# Revit family: NEC PA571W but PA550W before -DONE
name_source: partatom
category: Generic Models
revit_build: Autodesk Revit Architecture 2012 (Build: 20110309_2315(x64)
units: mm (PartAtom-declared; Revit-internal decimal feet)

## types (1)
- NEC PA571W but PA550W before -DONE
    Accessories - NP02CV = Terminal Cover
    Accessories - NP02LM1 = Wireless LAN module
    Accessories - NP11FL = 0.8 : 1 fixed short throw lens
    Accessories - NP12ZL = 1.19 - 1.56 : 1 zoom lens
    Accessories - NP13ZL = 1.5 - 3.0 : 1 zoom lens
    Accessories - NP14ZL = 2.97 - 4.79 : 1 zoom lens
    Accessories - NP15ZL = 4.7- 7.2 : 1 zoom lens
    Accessories - NP21LP = Replacement lamp
    Accessories - NP3250CM = Ceiling mount
    Accessories - PW RCRD-PJPX = Power Cable
    Accessories - RGBCBL-PJPX = RGB Cable
    Accessories - RMT-PJ33 = Remote remote control
    Accessories - SCP200 = Suspended ceiling plate
    Dimensions (W x D x H) = 19.6 x 14.1 x 5.7 in / 499 x 359 x 144 mm
    Environmental - Humidity = 20-80% non-condensing
    Environmental - Operational Temp = 41deg - 104degF / 5deg - 40degC
    Environmental - Storage = 14deg - 122degF / -10deg - 50degC
    Fan Noise = 38 dB normal / 31 dB eco
    Input Current = 5.1A
    Installation Orientation = Floor/Front, Floor/Rear, Ceiling/Front, Ceiling/Rear
    Manufacturer = NEC Display Solutions
    Model = PA500X
    Net Weight = 17.6 lb / 8 kg
    New Features = Portrait Orientation, Tilt free, 3D
    Optical - Contrast Ratio = 2000 : 1 with auto iris
    Optical - Display Technology = 0.75" LCD with MLA
    Optical - Lamp Life (up to) = 3000 hrs normal / 4000 hrs eco
    Optical - Lamp Type = 330W AC
    Optical - Lens F-number = F = 1.7 to 2.2, f = 24.4 to 32.5mm
    Optical - Lens Keystone Correction = +/- 40 deg horizontal, +/- 30 deg vertical
    Optical - Lens Shift = mechanical -0.1 to +0.6 vertical, +/-0.3 horizontal
    Optical - Lens Zoom = 1 to 1.33
    Optical - Lens focus = Manual
    Optical - Maximum Light Output (lumens) = 5700 Normal
    Optical - Projection Angle = 10.3 to 10.8deg tele / 13.7 to 14.5deg wide
    Optical - Projection Distance = 2.5 to 68.5ft, 0.74 to 20.9m
    Optical - Resolution, Native = WXGA 1280 x 800
    Optical - Screen Size (diagonal) = 25 to 500in, 635 to 12,700mm
    Optical - Throw Ratio = 1.5 to 3 (standard lens)
    Power Consumption (Normal/Eco Mode/Standby/Netwrok Standby/Power Saving) = 464W / 372W / 16W / 6W / 0.2W
    Power Requirements = 100-240V AC, 50/60Hz
    Regulations = USA UL 1950 FCC Class B, Canada CSA950 (C-UL), NOM
    Signal Compatibility/Connectivity - Audio = 10W mono
    Signal Compatibility/Connectivity - External Control = RS-232, IR
    Signal Compatibility/Connectivity - Input/Output Terminals  Audio = (2) L/R RCA, (3) mini stereo
    Signal Compatibility/Connectivity - Input/Output Terminals  Audio Out = mini VAO
    Signal Compatibility/Connectivity - Input/Output Terminals  Monitor Out = Yes
    Signal Compatibility/Connectivity - Input/Output Terminals  RGB1 (analog) = 15 pin
    Signal Compatibility/Connectivity - Input/Output Terminals  RGB2 (analog) = 15 pin
    Signal Compatibility/Connectivity - Input/Output Terminals  RGB3 (analog) = 5-BNC
    Signal Compatibility/Connectivity - Input/Output Terminals  RGB4 (digital) = Dual HDMI w/ HDCP
    Signal Compatibility/Connectivity - Input/Output Terminals  RGB5 (digital) = DisplayPort
    Signal Compatibility/Connectivity - Input/Output Terminals  Video 1 = RCA
    Signal Compatibility/Connectivity - Input/Output Terminals  Video 2 = S-Video
    Signal Compatibility/Connectivity - Macintosh Compatibility = Yes
    Signal Compatibility/Connectivity - PC Signal Compatibility = VGA, SVGA, XGA, SXGA, SXGA+, UXGA
    Signal Compatibility/Connectivity - SD/HD Video Signal Compatibility = 1080p, 1080i, 720p, 576p, 576i, 480p, 480i
    Signal Compatibility/Connectivity - Scan Rate = Horizontal 15-108 kHz / Vertical 48 - 120 Hz
    Signal Compatibility/Connectivity - Supported Video Standards = NTSC, NTSC4.43, PAL, PAL-60, PAL-M PAL-N, SECAM
    Signal Compatibility/Connectivity - Sync Compatibility = Separate Sync / Composite Sync / Sync on G
    URL = www.necdisplay.com
    Warranty Programs - ADVEXON1-1 = Extends term of InstaCare service program to 2 years
    Warranty Programs - ADVEXON2-1 = Extends term of InstaCare service program to 3 years
    Warranty Programs - NECECO = Projector recycling program, disposal certificate
    Warranty Programs - NECEW2-1 = Extends term of parts and labor warranty to 4 years

## geometry (parser evidence)
native form markers: Extrusion x1, Sweep x3
no freeform markers — native parametric forms only
